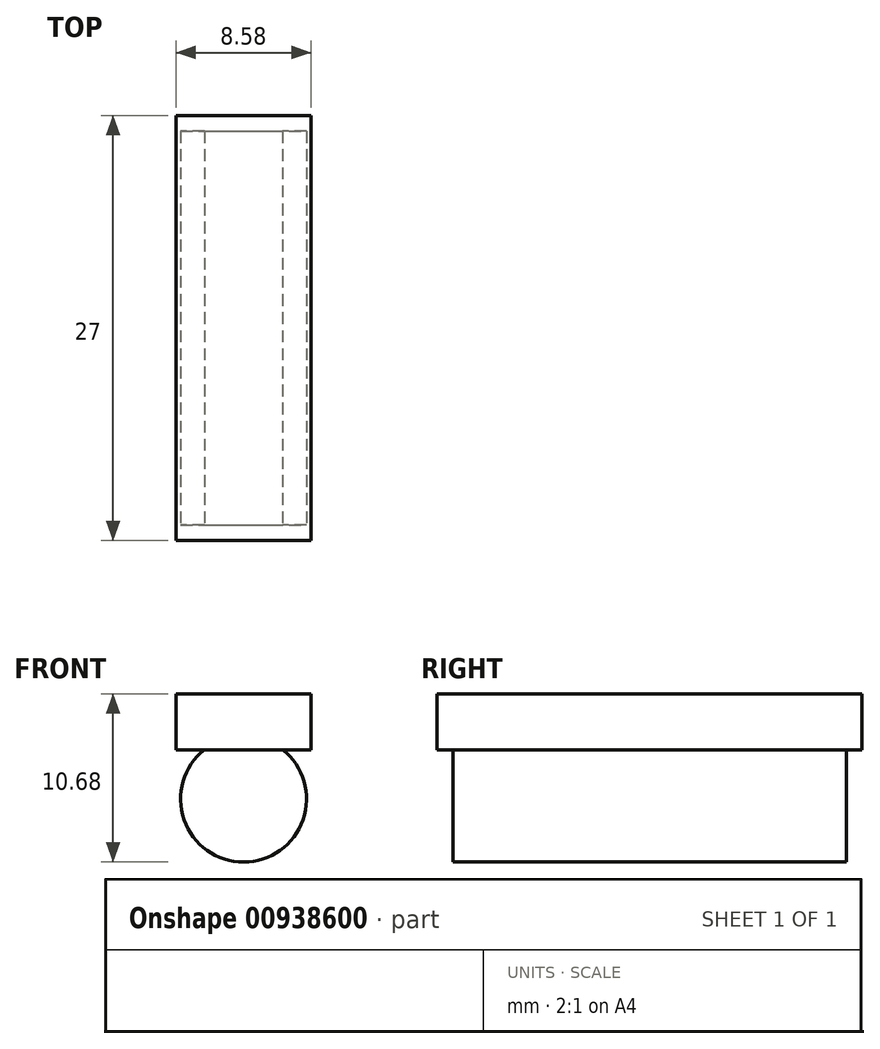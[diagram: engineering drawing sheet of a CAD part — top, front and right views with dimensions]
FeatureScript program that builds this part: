
annotation { "Feature Type Name" : "Feature", "Feature Type Description" : "" }
export const myFeature = defineFeature(function(context is Context, id is Id, definition is map)
    precondition{}
    {
        {
            var Q0;
            Q0=qCreatedBy(makeId("Front.planeOp"),FACE);
            var sketch = newSketch(context, id + "F0", { "sketchPlane" : qUnion([Q0])});
            skArc(sketch, "E0", {"start": v(-2.48, 3.14) * mm, "mid": v(0, -4) * mm, "end": v(2.48, 3.14) * mm});
            skLineSegment(sketch, "E1", {"start": v(-2.48, 3.14) * mm, "end": v(2.48, 3.14) * mm});
            skSolve(sketch);
        }
        {
            var Q0;
            Q0 = qSketchRegion(id + "F0", true);
            extrude(context, id + "F1", {"entities" : qUnion([Q0]), "oppositeDirection" : true, "depth" : 25 * mm, "offsetDistance" : 25 * mm});
        }
        {
            var Q0;
            Q0=makeQuery(id+"F1.opExtrude","CAP_FACE",FACE,{"disambiguationData":[OSD([sQuery(id+"F0.wireOp",EDGE,"E0"),sQuery(id+"F0.wireOp",EDGE,"E1")])],"isStart":true});
            var sketch = newSketch(context, id + "F2", { "sketchPlane" : qUnion([Q0])});
            skLineSegment(sketch, "E2.0", {"start": v(-2.48, 3.14) * mm, "end": v(2.48, 3.14) * mm});
            skArc(sketch, "E3", {"start": v(2.48, 3.14) * mm, "mid": v(1.78, 3.58) * mm, "end": v(1, 3.87) * mm});
            skLineSegment(sketch, "E4.top", {"start": v(1, 5.14) * mm, "end": v(-1, 5.14) * mm});
            skLineSegment(sketch, "E4.left", {"start": v(1, 3.87) * mm, "end": v(1, 5.14) * mm});
            skLineSegment(sketch, "E4.right", {"start": v(-1, 3.87) * mm, "end": v(-1, 5.14) * mm});
            skPoint(sketch, "E4.middle", {"position": v(0, 3.14) * mm});
            skPoint(sketch, "E4.bottom.end.orphan", {"position": v(-1, 1.14) * mm});
            skPoint(sketch, "E5.orphan", {"position": v(1, 1.14) * mm});
            skArc(sketch, "E6.trimOffspring", {"start": v(-1, 3.87) * mm, "mid": v(-1.78, 3.58) * mm, "end": v(-2.48, 3.14) * mm});
            skSolve(sketch);
        }
        {
            var Q0;
            Q0 = qSketchRegion(id + "F2", true);
            extrude(context, id + "F3", {"entities" : qUnion([Q0]), "oppositeDirection" : true, "depth" : 25 * mm, "offsetDistance" : 25 * mm});
        }
        {
            var Q0;
            Q0=makeQuery(id+"F3.opExtrude","CAP_FACE",FACE,{"disambiguationData":[OSD([sQuery(id+"F2.wireOp",EDGE,"E2.0"),sQuery(id+"F2.wireOp",EDGE,"E3"),sQuery(id+"F2.wireOp",EDGE,"E4.top"),sQuery(id+"F2.wireOp",EDGE,"E4.left"),sQuery(id+"F2.wireOp",EDGE,"E4.right"),sQuery(id+"F2.wireOp",EDGE,"E6.trimOffspring")])],"isStart":true});
            var sketch = newSketch(context, id + "F4", { "sketchPlane" : qUnion([Q0])});
            skLineSegment(sketch, "E7.0.0", {"start": v(-1, 5.14) * mm, "end": v(-1, 3.87) * mm});
            skArc(sketch, "E7.0.1", {"start": v(-1, 3.87) * mm, "mid": v(-1.78, 3.58) * mm, "end": v(-2.48, 3.14) * mm});
            skArc(sketch, "E7.0.3", {"start": v(2.48, 3.14) * mm, "mid": v(1.78, 3.58) * mm, "end": v(1, 3.87) * mm});
            skLineSegment(sketch, "E7.0.4", {"start": v(1, 3.87) * mm, "end": v(1, 5.14) * mm});
            skLineSegment(sketch, "E7.0.5", {"start": v(1, 5.14) * mm, "end": v(-1, 5.14) * mm});
            skLineSegment(sketch, "E8", {"start": v(-2.48, 3.14) * mm, "end": v(-4.3, 3.14) * mm});
            skLineSegment(sketch, "E9", {"start": v(-4.3, 3.14) * mm, "end": v(-4.3, 6.68) * mm});
            skLineSegment(sketch, "E10", {"start": v(-4.3, 6.68) * mm, "end": v(0, 6.68) * mm});
            skLineSegment(sketch, "E11", {"start": v(0, 6.68) * mm, "end": v(0, 3.14) * mm, "construction": true});
            skLineSegment(sketch, "E12.MirrorCS", {"start": v(4.3, 6.68) * mm, "end": v(0, 6.68) * mm});
            skLineSegment(sketch, "E13.MirrorCS", {"start": v(4.3, 3.14) * mm, "end": v(4.3, 6.68) * mm});
            skLineSegment(sketch, "E14.MirrorCS", {"start": v(2.48, 3.14) * mm, "end": v(4.3, 3.14) * mm});
            skSolve(sketch);
        }
        {
            var Q0;
            Q0 = qSketchRegion(id + "F4", true);
            extrude(context, id + "F5", {"entities" : qUnion([Q0]), "oppositeDirection" : true, "depth" : 25 * mm, "offsetDistance" : 25 * mm});
        }
        {
            var Q0;
            Q0=makeQuery(id+"F5.opExtrude","SWEPT_FACE",FACE,{"disambiguationData":[OSD([sQuery(id+"F4.wireOp",EDGE,"E8")])]});
            var sketch = newSketch(context, id + "F6", { "sketchPlane" : qUnion([Q0])});
            skLineSegment(sketch, "E15.0", {"start": v(-2.48, 0) * mm, "end": v(-4.3, 0) * mm});
            skLineSegment(sketch, "E16.0", {"start": v(-2.48, 0) * mm, "end": v(2.48, 0) * mm});
            skLineSegment(sketch, "E17.0", {"start": v(2.48, 0) * mm, "end": v(4.3, 0) * mm});
            skLineSegment(sketch, "E18.0", {"start": v(-2.48, -25) * mm, "end": v(-4.3, -25) * mm});
            skLineSegment(sketch, "E19.0", {"start": v(-2.48, -25) * mm, "end": v(2.48, -25) * mm});
            skLineSegment(sketch, "E20.0", {"start": v(2.48, -25) * mm, "end": v(4.3, -25) * mm});
            skLineSegment(sketch, "E21.bottom", {"start": v(-4.3, 0) * mm, "end": v(4.3, 0) * mm});
            skLineSegment(sketch, "E21.top", {"start": v(-4.3, 1) * mm, "end": v(4.3, 1) * mm});
            skLineSegment(sketch, "E21.left", {"start": v(-4.3, 0) * mm, "end": v(-4.3, 1) * mm});
            skLineSegment(sketch, "E21.right", {"start": v(4.3, 0) * mm, "end": v(4.3, 1) * mm});
            skLineSegment(sketch, "E22.bottom", {"start": v(-4.3, -25) * mm, "end": v(4.3, -25) * mm});
            skLineSegment(sketch, "E22.top", {"start": v(-4.3, -26) * mm, "end": v(4.3, -26) * mm});
            skLineSegment(sketch, "E22.left", {"start": v(-4.3, -25) * mm, "end": v(-4.3, -26) * mm});
            skLineSegment(sketch, "E22.right", {"start": v(4.3, -25) * mm, "end": v(4.3, -26) * mm});
            skSolve(sketch);
        }
        {
            var Q0;
            Q0 = qSketchRegion(id + "F6", true);
            var Q1;
            Q1=makeQuery(id+"F5.opExtrude","SWEPT_FACE",FACE,{"disambiguationData":[OSD([sQuery(id+"F4.wireOp",EDGE,"E10"),sQuery(id+"F4.wireOp",EDGE,"E12.MirrorCS")])]});
            extrude(context, id + "F7", {"entities" : qUnion([Q0]), "operationType" : NewBodyOperationType.ADD, "endBound" : BoundingType.UP_TO_SURFACE, "oppositeDirection" : true, "depth" : 25 * mm, "endBoundEntityFace" : qUnion([Q1]), "offsetDistance" : 25 * mm});
        }
    });
